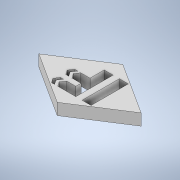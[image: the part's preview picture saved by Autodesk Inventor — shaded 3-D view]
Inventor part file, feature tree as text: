
AUTODESK INVENTOR PART (.ipt)
format: ipt  version: 2020 (Build 240168000, 168)  size: 198,656 bytes
history: native  units: in
note: dims shown in document units (in); Inventor stores cm internally (conversion verified against a paired STEP export)
features: sketch x2, extrude x1, other x1
ambient origin geometry x8: Origin, YZ Plane, XZ Plane, XY Plane, X Axis, Y Axis, Z Axis, Center Point
bodies: Solid1 (feature_tree)
feature tree (4):
  sketch  "Sketch1"  dims[d1=0.45in d3=0.45in]
  extrude  "Extrusion1"  Depth=0.45in
  other  "Image1"
  sketch  "Sketch2"  dims[d4=0.8589in d5=90.0deg d6=1.5in d7=0.0in]
